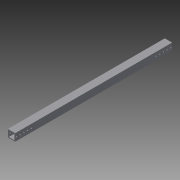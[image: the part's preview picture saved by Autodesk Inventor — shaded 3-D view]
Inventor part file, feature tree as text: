
AUTODESK INVENTOR PART (.ipt)
format: ipt  version: 2014 (Build 180170000, 170)  size: 104,448 bytes
history: native  units: in
note: dims shown in document units (in); Inventor stores cm internally (conversion verified against a paired STEP export)
features: extrude x2, sketch x2
ambient origin geometry x8: Origin, YZ Plane, XZ Plane, XY Plane, X Axis, Y Axis, Z Axis, Center Point
bodies: Solid1 (feature_tree)
feature tree (4):
  extrude  "Extrusion1"  Depth=1.0in
  extrude  "Extrusion2"  Depth=21.375in TaperAngle=0.0deg
  sketch  "Sketch1"  dims[d0=1.0in d1=1.0in]
  sketch  "Sketch2"  dims[d2=0.125in d3=21.375in d4=0.0in d5=0.163in d6=0.1875in d7=0.5in d8=1.9685in d10=0.5in d11=0.3937in d13=1.0in d15=23.375in d16=0.0in]
